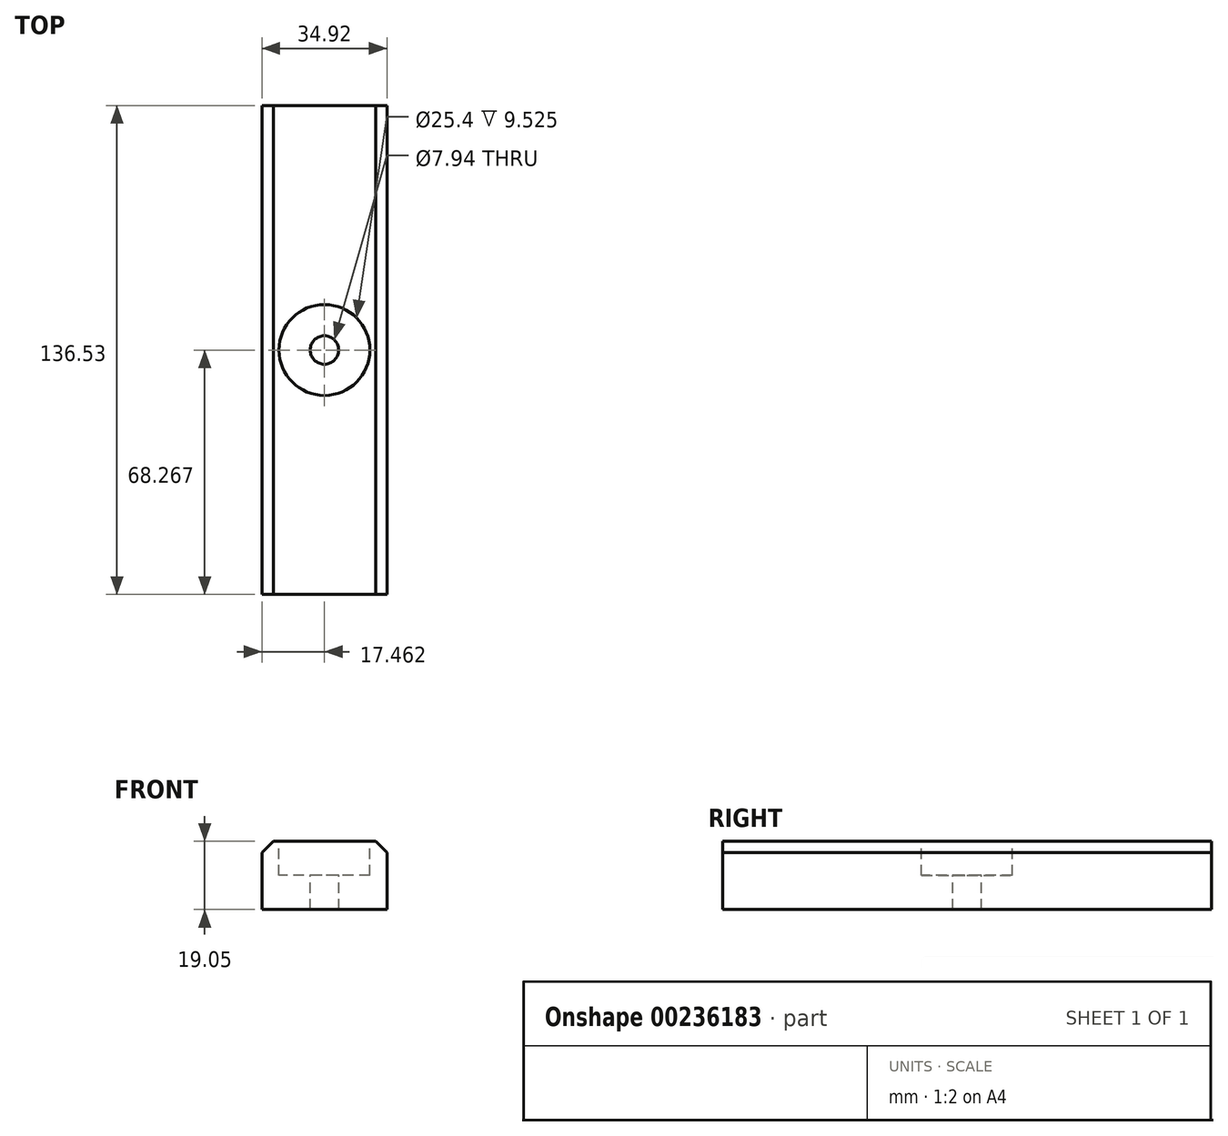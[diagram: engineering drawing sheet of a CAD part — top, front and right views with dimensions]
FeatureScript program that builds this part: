
annotation { "Feature Type Name" : "Feature", "Feature Type Description" : "" }
export const myFeature = defineFeature(function(context is Context, id is Id, definition is map)
    precondition{}
    {
        {
            var Q0;
            Q0=qCreatedBy(makeId("Front.planeOp"),FACE);
            var sketch = newSketch(context, id + "F0", { "sketchPlane" : qUnion([Q0])});
            skLineSegment(sketch, "E0.bottom", {"start": v(0, 0) * mm, "end": v(34.93, 0) * mm});
            skLineSegment(sketch, "E0.top", {"start": v(0, -19.05) * mm, "end": v(34.93, -19.05) * mm});
            skLineSegment(sketch, "E0.left", {"start": v(0, 0) * mm, "end": v(0, -19.05) * mm});
            skLineSegment(sketch, "E0.right", {"start": v(34.93, 0) * mm, "end": v(34.93, -19.05) * mm});
            skSolve(sketch);
        }
        {
            var Q0;
            Q0=makeQuery(id+"F0.imprint","IMPRINT",FACE,{"disambiguationData":[TD([[makeQuery(id+"F0.imprint","IMPRINT",EDGE,{"derivedFrom":sQuery(id+"F0.wireOp",EDGE,"E0.bottom")}),-1.0]])]});
            extrude(context, id + "F1", {"entities" : qUnion([Q0]), "depth" : 136.53 * mm});
        }
        {
            var Q0;
            Q0=makeQuery(id+"F1.opExtrude","SWEPT_EDGE",EDGE,{"disambiguationData":[OSD([sQuery(id+"F0.wireOp",EDGE,"E0.bottom"),sQuery(id+"F0.wireOp",EDGE,"E0.right")])]});
            var Q1;
            Q1=makeQuery(id+"F1.opExtrude","SWEPT_EDGE",EDGE,{"disambiguationData":[OSD([sQuery(id+"F0.wireOp",EDGE,"E0.bottom"),sQuery(id+"F0.wireOp",EDGE,"E0.left")])]});
            chamfer(context, id + "F2", {"entities" : qUnion([Q0, Q1]), "width" : 3.17 * mm, "tangentPropagation" : true});
        }
        {
            var Q0;
            Q0=makeQuery(id+"F1.opExtrude","SWEPT_FACE",FACE,{"disambiguationData":[OSD([sQuery(id+"F0.wireOp",EDGE,"E0.bottom")])]});
            var sketch = newSketch(context, id + "F3", { "sketchPlane" : qUnion([Q0])});
            skCircle(sketch, "E1", {"center": v(17.46, -68.26) * mm, "radius": 12.7 * mm});
            skPoint(sketch, "E1.centerSnap0", {"position": v(17.46, 0) * mm});
            skPoint(sketch, "E1.centerSnap1", {"position": v(31.75, -68.26) * mm});
            skSolve(sketch);
        }
        {
            var Q0;
            Q0=makeQuery(id+"F3.imprint","IMPRINT",FACE,{"disambiguationData":[TD([[makeQuery(id+"F3.imprint","IMPRINT",EDGE,{"derivedFrom":sQuery(id+"F3.wireOp",EDGE,"E1")}),1.0]])]});
            extrude(context, id + "F4", {"entities" : qUnion([Q0]), "operationType" : NewBodyOperationType.REMOVE, "oppositeDirection" : true, "depth" : 9.52 * mm});
        }
        {
            var Q0;
            Q0=makeQuery(id+"F4.boolean.opBoolean","COPY",FACE,{"derivedFrom":makeQuery(id+"F4.opExtrude","CAP_FACE",FACE,{"disambiguationData":[OSD([sQuery(id+"F3.wireOp",EDGE,"E1")])],"isStart":false})});
            var sketch = newSketch(context, id + "F5", { "sketchPlane" : qUnion([Q0])});
            skCircle(sketch, "E2", {"center": v(17.46, -68.26) * mm, "radius": 3.97 * mm});
            skSolve(sketch);
        }
        {
            var Q0;
            Q0=makeQuery(id+"F5.imprint","IMPRINT",FACE,{"disambiguationData":[TD([[makeQuery(id+"F5.imprint","IMPRINT",EDGE,{"derivedFrom":sQuery(id+"F5.wireOp",EDGE,"E2")}),1.0]])]});
            extrude(context, id + "F6", {"entities" : qUnion([Q0]), "operationType" : NewBodyOperationType.REMOVE, "oppositeDirection" : true, "depth" : 25.4 * mm});
        }
    });
